# Revit family: LEGRAND_TOMAS SIN ENCLAVAMIENTO_EMPOTRADAS_IP66_230
name_source: partatom
category: Installations électriques
revit_build: Autodesk Revit 2018 (Build: 20170223_1515(x64)
units: mm (PartAtom-declared; Revit-internal decimal feet)

## family parameters
Conserver l'orientation des annotations = Non
Cote de connecteur circulaire = Utiliser le diamètre
Couper avec des vides une fois chargée = Non
Hôte = Face
Partagée = Non
Point de calcul de pièce = Non
Type d'élément = Normal

## types (9) — shared parameters
Condiciones Generales de Uso = https://export.legrand.com
Description = Toma AL estándar internacional para montaje empotrado o en superficie con accesorio permite la alimentación de aparatos de potencia
Elévation par défaut = 1000 mm  [stored 3.28084 ft]
Fabricant = Legrand
Temperatura maxima de instalación = 40°C
Temperatura maxima de uso = 100°C
Temperatura minima de instalación = -20°C
Temperatura minima de uso = -50°C
Tension V = 230 V  50/60 Hz azul
clase de protección IP = IP66/67-55
color característico = azul
instalación de empotrar E o de superficie S = empotrar y superficie
materia de la caja = plástico
resistencia a los choques IK = 09
sin halogeno = Non
tipo de conexión = conexión por tonillo

## per-type parameters (varying)
| type | Dia bouchon | Estándar CEI o NFC | Modèle | RAY BOUCHON | Ray | altura mm | ancho mm | dIA | distancia de fijación horizontal mm | distancia de fijación vertical mm | h1 | intensidad A | numero de polos | posición de la tierra h | profundidad de empotrar mm | profundidad mm |
| base para cuadro Hypra   IP66/67-55   16 A   200/250 V   2P+T   plast | 68 mm | CEI | 051126 | 34 mm | 21 mm  [stored 0.0688976 ft] | 72 mm | 64 mm | 42 mm | 52 mm | 60 mm | 43 mm | 16 A | 3 | 6 | 40 mm | 85 mm |
| base para cuadro Hypra   IP66/67-55   16 A   200/250 V   3P+T   plast | 79 mm | CEI | 051127 | 40 mm | 24 mm | 84 mm | 74 mm | 49 mm | 60 mm | 70 mm | 50 mm | 16 A | 6 | 6 | 41 mm | 89 mm  [stored 0.291995 ft] |
| base para cuadro entreejes unificados Hypra  IP66/67-55  16 A   200/250 V   2P+T   plast | 84 mm | CEI | 051146 | 42 mm | 26 mm | 84 mm | 84 mm | 52 mm | 70 mm | 70 mm | 50 mm | 16 A | 3 | 6 | 42 mm | 81 mm |
| base para cuadro entreejes unificados Hypra  IP66/67-55  16 A   200/250 V   3P+T   plast | 84 mm | CEI | 051147 | 42 mm | 26 mm | 84 mm | 84 mm | 52 mm | 70 mm | 70 mm | 50 mm | 16 A | 4 | 9 | 43 mm | 84 mm |
| base para cuadro entreejes unificados Hypra  IP66/67-55  32 A   200 250 V   2P+T   plast | 89 mm  [stored 0.291995 ft] | CEI | 053046 | 45 mm | 27 mm | 94 mm | 84 mm | 55 mm | 70 mm | 70 mm | 56 mm | 32 A | 3 | 6 | 54 mm | 104 mm |
| base para cuadro entreejes unificados Hypra  IP66/67-55  32 A   230 V   3P+T   plast | 89 mm  [stored 0.291995 ft] | CEI | 053047 | 45 mm | 27 mm | 94 mm | 84 mm | 55 mm | 70 mm | 70 mm | 56 mm | 32 A | 4 | 9 | 54 mm | 104 mm |
| base para cuadro Hypra   IP66/67-55  16 A   250 V   2P+T   estandar domestico   plast | 67 mm | NFC | 053911 | 34 mm | 21 mm  [stored 0.0688976 ft] | 67 mm | 67 mm | 41 mm | 55 mm | 55 mm | 40 mm | 16 A | 3 | 6 | 15 mm | 63 mm  [stored 0.206693 ft] |
| base para cuadro Hypra  IP66/67-55   63A   200 250 V   2P+T   plast | 106 mm | CEI | 059326 | 53 mm | 33 mm | 106 mm | 106 mm | 65 mm | 77 mm | 85 mm | 64 mm | 63 A | 3 | 6 | 85 mm | 164 mm |
| base para cuadro Hypra  IP66/67-55  63 A    230 V   3P+T   plast | 106 mm | CEI | 059327 | 53 mm | 33 mm | 106 mm | 106 mm | 65 mm | 77 mm | 85 mm | 64 mm | 63 A | 4 | 9 | 85 mm | 164 mm |

note: [stored X ft] marks values corroborated as IEEE doubles in the binary element streams (Revit-internal decimal feet)
